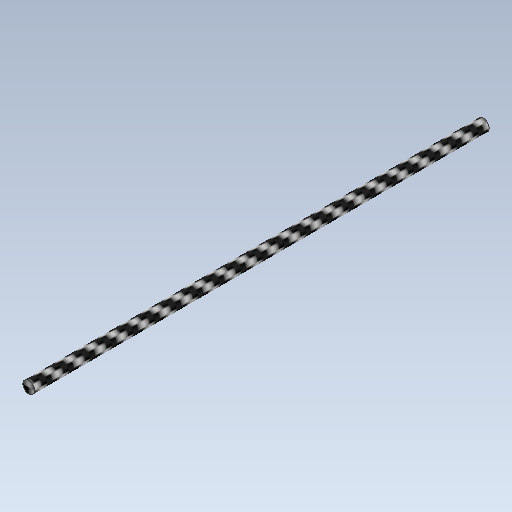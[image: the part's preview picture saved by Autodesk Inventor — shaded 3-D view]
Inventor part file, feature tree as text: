
AUTODESK INVENTOR PART (.ipt)
format: ipt  version: 2020 (Build 240168000, 168)  size: 105,984 bytes
history: native  units: in
note: dims shown in document units (in); Inventor stores cm internally (conversion verified against a paired STEP export)
features: extrude x1, sketch x1
ambient origin geometry x8: Origin, YZ Plane, XZ Plane, XY Plane, X Axis, Y Axis, Z Axis, Center Point
bodies: Solid1 (feature_tree)
feature tree (2):
  extrude  "Extrusion1"  Depth=3.1106in
  sketch  "Sketch1"  dims[d0=0.0827in d1=3.1106in d2=0.0in]
